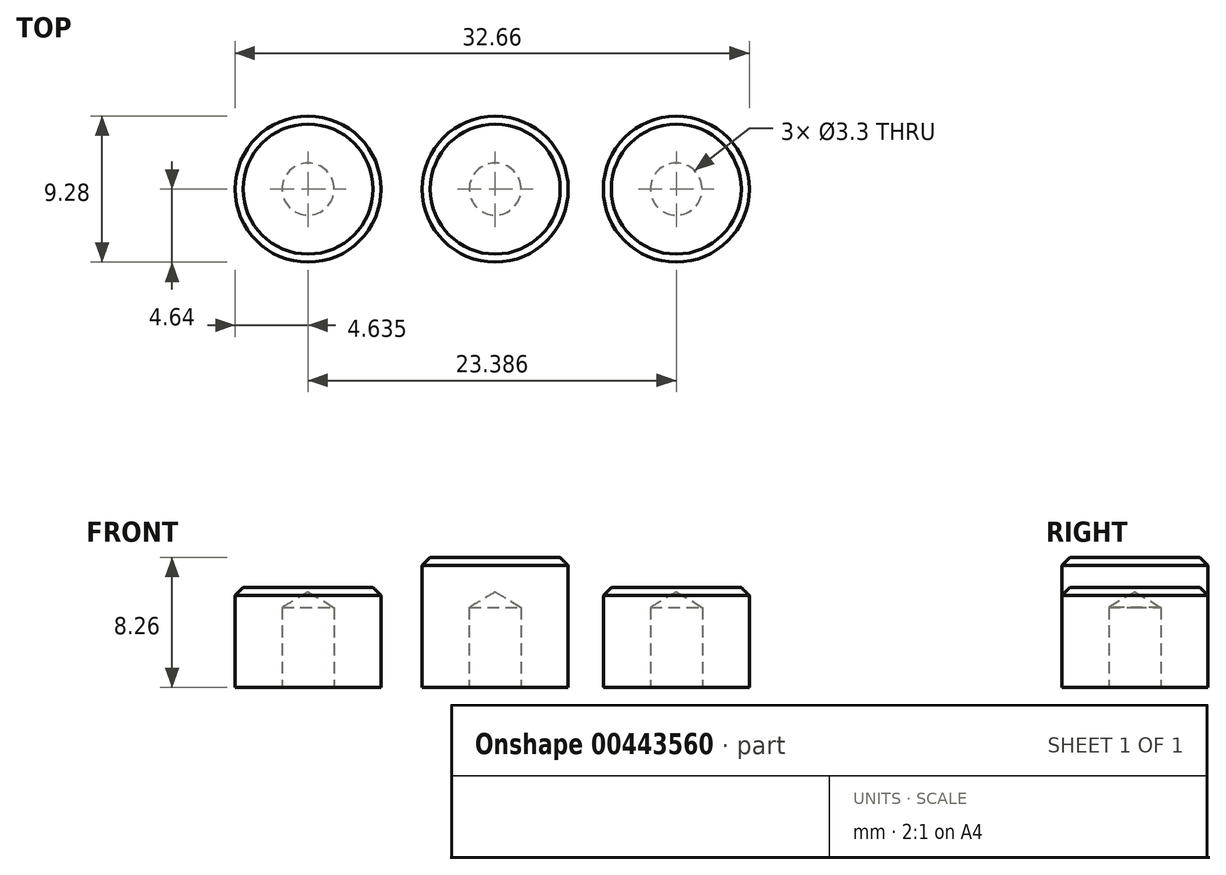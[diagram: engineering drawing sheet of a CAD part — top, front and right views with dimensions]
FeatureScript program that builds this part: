
annotation { "Feature Type Name" : "Feature", "Feature Type Description" : "" }
export const myFeature = defineFeature(function(context is Context, id is Id, definition is map)
    precondition{}
    {
        {
            var Q0;
            Q0=qCreatedBy(makeId("Top.planeOp"),FACE);
            var sketch = newSketch(context, id + "F0", { "sketchPlane" : qUnion([Q0])});
            skCircle(sketch, "E0", {"center": v(0, 0) * mm, "radius": 4.64 * mm});
            skLineSegment(sketch, "E1", {"start": v(-4.64, 0) * mm, "end": v(4.64, 0) * mm});
            skCircle(sketch, "E2", {"center": v(11.5, 0) * mm, "radius": 4.64 * mm});
            skCircle(sketch, "E3", {"center": v(-11.89, 0) * mm, "radius": 4.64 * mm});
            skSolve(sketch);
        }
        {
            var Q0;
            Q0=makeQuery(id+"F0.imprint","IMPRINT",FACE,{"disambiguationData":[TD([[makeQuery(id+"F0.imprint","IMPRINT",EDGE,{"derivedFrom":sQuery(id+"F0.wireOp",EDGE,"E3")}),1.0]])]});
            var Q1;
            Q1=makeQuery(id+"F0.imprint","IMPRINT",FACE,{"disambiguationData":[TD([[makeQuery(id+"F0.imprint","IMPRINT",EDGE,{"derivedFrom":sQuery(id+"F0.wireOp",EDGE,"E2")}),1.0]])]});
            extrude(context, id + "F1", {"entities" : qUnion([Q0, Q1]), "depth" : 6.35 * mm});
        }
        {
            var Q0;
            {var subQ0=sQuery(id+"F0.wireOp",EDGE,"E1");Q0=makeQuery(id+"F0.imprint","IMPRINT",FACE,{"disambiguationData":[TD([[makeQuery(id+"F0.imprint","IMPRINT",EDGE,{"derivedFrom":subQ0}),-1.0]])]});}
            var Q1;
            {var subQ0=sQuery(id+"F0.wireOp",EDGE,"E1");Q1=makeQuery(id+"F0.imprint","IMPRINT",FACE,{"disambiguationData":[TD([[makeQuery(id+"F0.imprint","IMPRINT",EDGE,{"derivedFrom":subQ0}),1.0]])]});}
            extrude(context, id + "F2", {"entities" : qUnion([Q0, Q1]), "depth" : 8.25 * mm});
        }
        {
            var Q0;
            Q0=makeQuery(id+"F1.opExtrude","CAP_FACE",FACE,{"disambiguationData":[OSD([sQuery(id+"F0.wireOp",EDGE,"E3")])],"isStart":false});
            var Q1;
            Q1=makeQuery(id+"F2.opExtrude","CAP_FACE",FACE,{"disambiguationData":[OSD([sQuery(id+"F0.wireOp",EDGE,"E0")])],"isStart":false});
            var Q2;
            Q2=makeQuery(id+"F1.opExtrude","CAP_FACE",FACE,{"disambiguationData":[OSD([sQuery(id+"F0.wireOp",EDGE,"E2")])],"isStart":false});
            chamfer(context, id + "F3", {"entities" : qUnion([Q0, Q1, Q2]), "width" : 0.5 * mm, "tangentPropagation" : true});
        }
        {
            var Q0;
            Q0=sQuery(id+"F0.wireOp",VERTEX,"E3.center");
            var Q1;
            Q1=sQuery(id+"F0.wireOp",VERTEX,"E0.center");
            var Q2;
            Q2=sQuery(id+"F0.wireOp",VERTEX,"E2.center");
            var Q3;
            Q3=makeQuery(id+"F1.opExtrude","SWEPT_BODY",BODY,{"disambiguationData":[OSD([sQuery(id+"F0.wireOp",EDGE,"E3")])]});
            var Q4;
            Q4=makeQuery(id+"F2.opExtrude","SWEPT_BODY",BODY,{"disambiguationData":[OSD([sQuery(id+"F0.wireOp",EDGE,"E0")])]});
            var Q5;
            Q5=makeQuery(id+"F1.opExtrude","SWEPT_BODY",BODY,{"disambiguationData":[OSD([sQuery(id+"F0.wireOp",EDGE,"E2")])]});
            hole(context, id + "F4", {"style" : HoleStyle.SIMPLE, "endStyle" : HoleEndStyle.BLIND, "oppositeDirection" : true, "holeDiameter" : 3.3 * mm, "holeDepth" : 5.08 * mm, "isTappedThrough" : true, "tappedDepth" : 12.7 * mm, "tapClearance" : 3, "locations" : qUnion([Q0, Q1, Q2]), "scope" : qUnion([Q3, Q4, Q5])});
        }
    });
